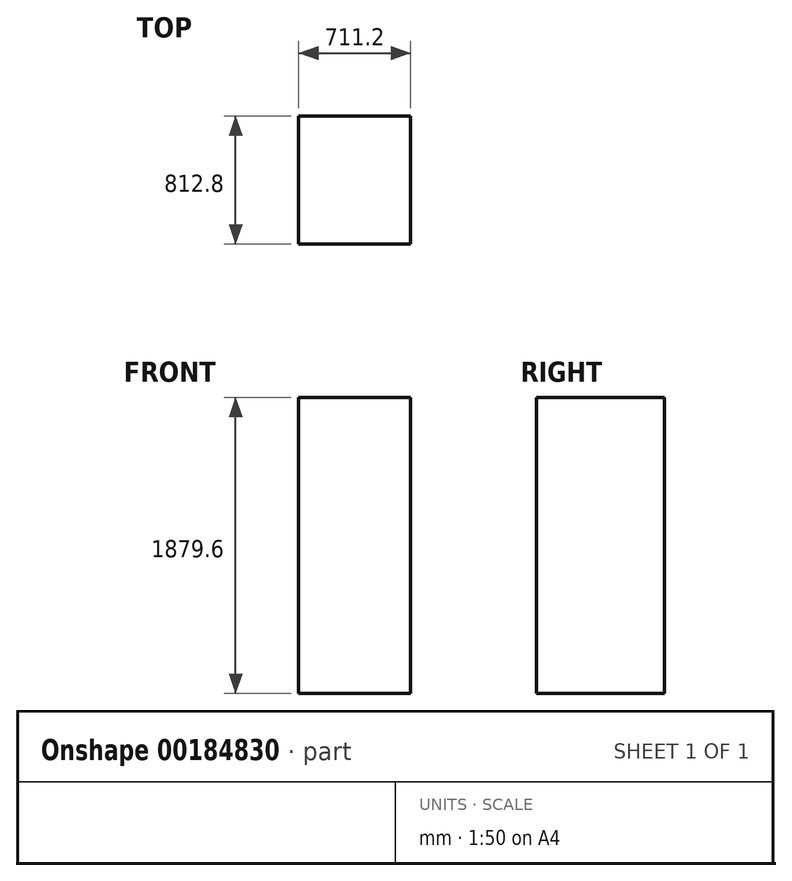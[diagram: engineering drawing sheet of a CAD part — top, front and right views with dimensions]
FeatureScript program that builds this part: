
annotation { "Feature Type Name" : "Feature", "Feature Type Description" : "" }
export const myFeature = defineFeature(function(context is Context, id is Id, definition is map)
    precondition{}
    {
        {
            var Q0;
            Q0=qCreatedBy(makeId("Top.planeOp"),FACE);
            var sketch = newSketch(context, id + "F0", { "sketchPlane" : qUnion([Q0])});
            skLineSegment(sketch, "E0.bottom", {"start": v(355.6, -406.4) * mm, "end": v(-355.6, -406.4) * mm});
            skLineSegment(sketch, "E0.top", {"start": v(355.6, 406.4) * mm, "end": v(-355.6, 406.4) * mm});
            skLineSegment(sketch, "E0.left", {"start": v(355.6, -406.4) * mm, "end": v(355.6, 406.4) * mm});
            skLineSegment(sketch, "E0.right", {"start": v(-355.6, -406.4) * mm, "end": v(-355.6, 406.4) * mm});
            skPoint(sketch, "E0.middle", {"position": v(0, 0) * mm});
            skSolve(sketch);
        }
        {
            var Q0;
            Q0=makeQuery(id+"F0.imprint","IMPRINT",FACE,{"disambiguationData":[TD([[makeQuery(id+"F0.imprint","IMPRINT",EDGE,{"derivedFrom":sQuery(id+"F0.wireOp",EDGE,"E0.bottom")}),-1.0]])]});
            extrude(context, id + "F1", {"entities" : qUnion([Q0]), "depth" : 1879.6 * mm});
        }
    });
